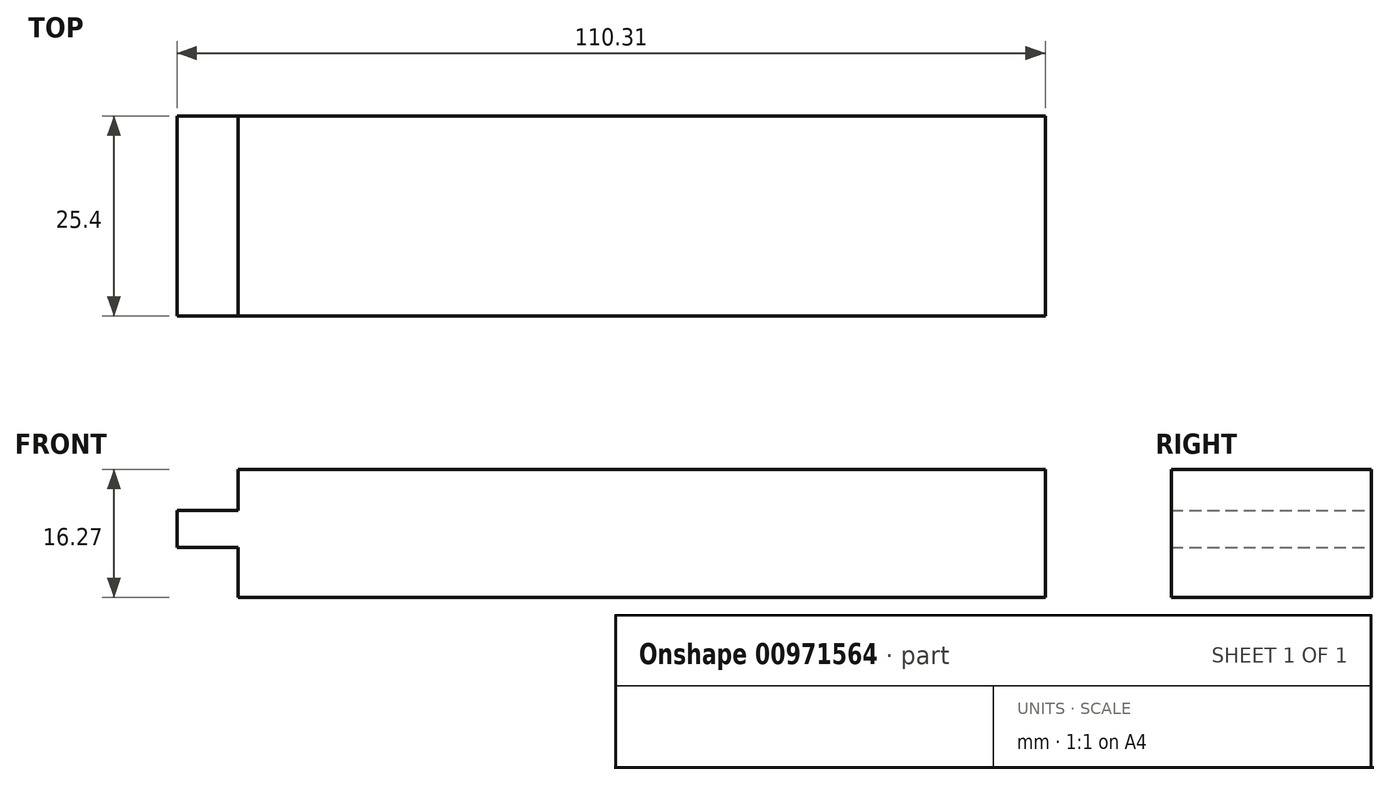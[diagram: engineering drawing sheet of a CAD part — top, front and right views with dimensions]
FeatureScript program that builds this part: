
annotation { "Feature Type Name" : "Feature", "Feature Type Description" : "" }
export const myFeature = defineFeature(function(context is Context, id is Id, definition is map)
    precondition{}
    {
        {
            var Q0;
            Q0=qCreatedBy(makeId("Front.planeOp"),FACE);
            var sketch = newSketch(context, id + "F0", { "sketchPlane" : qUnion([Q0])});
            skLineSegment(sketch, "E0.bottom", {"start": v(-46.55, 32.58) * mm, "end": v(-32.41, 32.58) * mm});
            skLineSegment(sketch, "E0.top", {"start": v(-46.55, 37.29) * mm, "end": v(-32.41, 37.29) * mm});
            skLineSegment(sketch, "E0.left", {"start": v(-46.55, 32.58) * mm, "end": v(-46.55, 37.29) * mm});
            skLineSegment(sketch, "E0.right", {"start": v(-32.41, 32.58) * mm, "end": v(-32.41, 37.29) * mm});
            skLineSegment(sketch, "E1.bottom", {"start": v(-38.78, 26.21) * mm, "end": v(63.76, 26.21) * mm});
            skLineSegment(sketch, "E1.top", {"start": v(-38.78, 42.48) * mm, "end": v(63.76, 42.48) * mm});
            skLineSegment(sketch, "E1.left", {"start": v(-38.78, 26.21) * mm, "end": v(-38.78, 42.48) * mm});
            skLineSegment(sketch, "E1.right", {"start": v(63.76, 26.21) * mm, "end": v(63.76, 42.48) * mm});
            skSolve(sketch);
        }
        {
            var Q0;
            Q0 = qSketchRegion(id + "F0", true);
            extrude(context, id + "F1", {"entities" : qUnion([Q0]), "depth" : 25.4 * mm, "offsetDistance" : 25.4 * mm});
        }
    });
